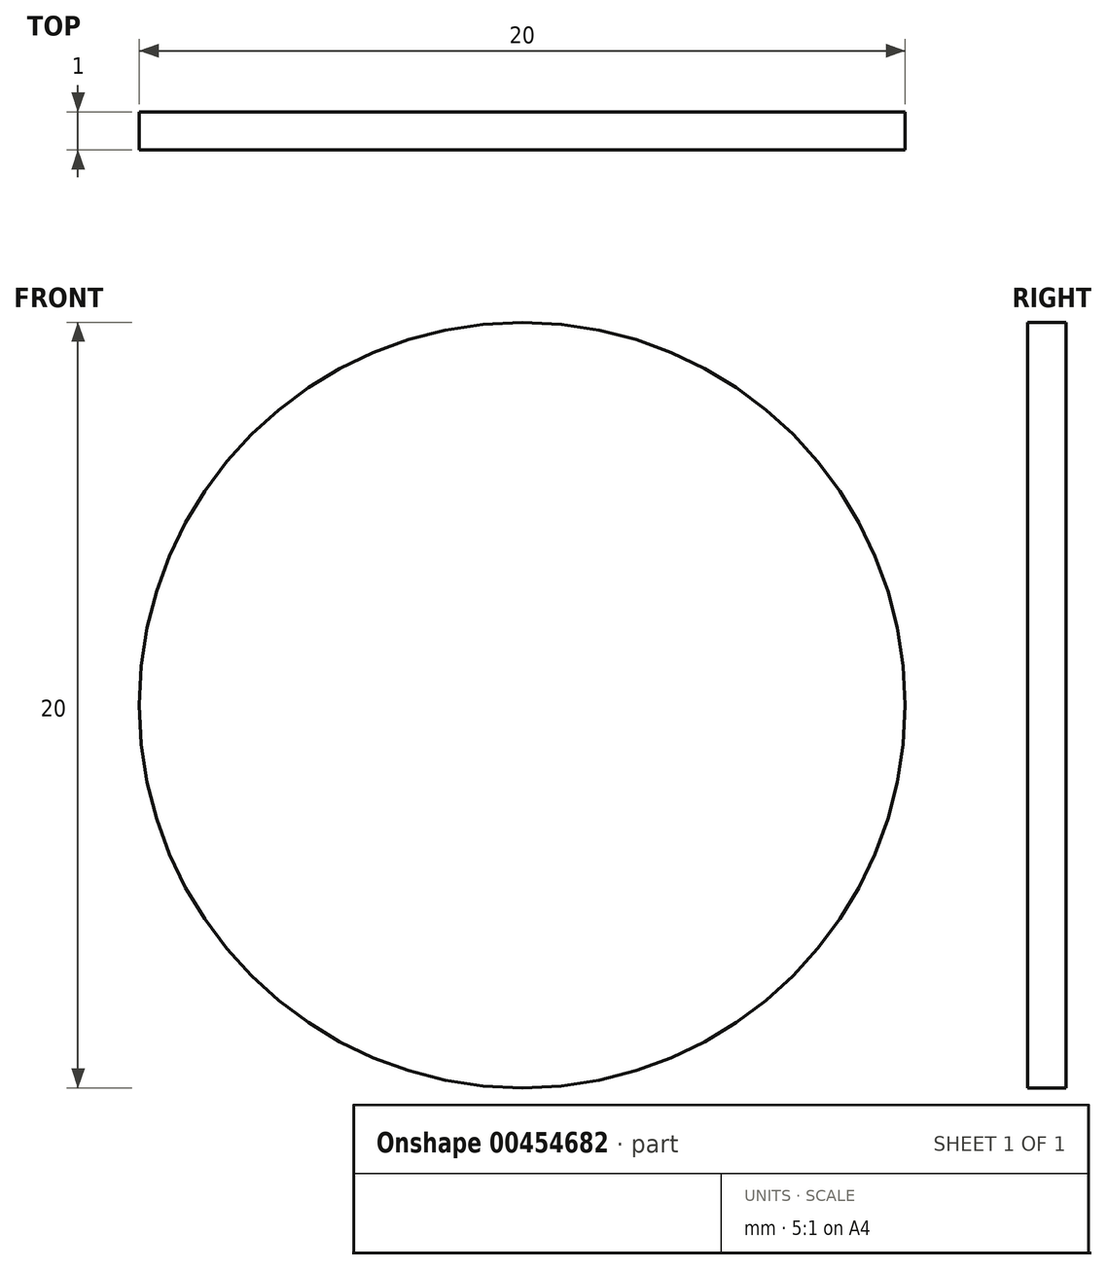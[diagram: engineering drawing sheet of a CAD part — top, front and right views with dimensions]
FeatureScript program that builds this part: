
annotation { "Feature Type Name" : "Feature", "Feature Type Description" : "" }
export const myFeature = defineFeature(function(context is Context, id is Id, definition is map)
    precondition{}
    {
        {
            var Q0;
            Q0=qCreatedBy(makeId("Right.planeOp"),FACE);
            var sketch = newSketch(context, id + "F0", { "sketchPlane" : qUnion([Q0])});
            skLineSegment(sketch, "E0.bottom", {"start": v(0, 0) * mm, "end": v(1, 0) * mm});
            skLineSegment(sketch, "E0.top", {"start": v(0, 10) * mm, "end": v(1, 10) * mm});
            skLineSegment(sketch, "E0.left", {"start": v(0, 0) * mm, "end": v(0, 10) * mm});
            skLineSegment(sketch, "E0.right", {"start": v(1, 0) * mm, "end": v(1, 10) * mm});
            skSolve(sketch);
        }
        {
            var Q0;
            Q0=qCreatedBy(makeId("Right.planeOp"),FACE);
            var sketch = newSketch(context, id + "F1", { "sketchPlane" : qUnion([Q0])});
            skLineSegment(sketch, "E1", {"start": v(-9.78, 0) * mm, "end": v(9.97, 0) * mm, "construction": true});
            skSolve(sketch);
        }
        {
            var Q0;
            Q0 = qSketchRegion(id + "F0", true);
            var Q1;
            Q1=sQuery(id+"F1.wireOp",EDGE,"E1");
            revolve(context, id + "F2", {"entities" : qUnion([Q0]), "axis" : qUnion([Q1]), "revolveType" : RevolveType.FULL});
        }
    });
